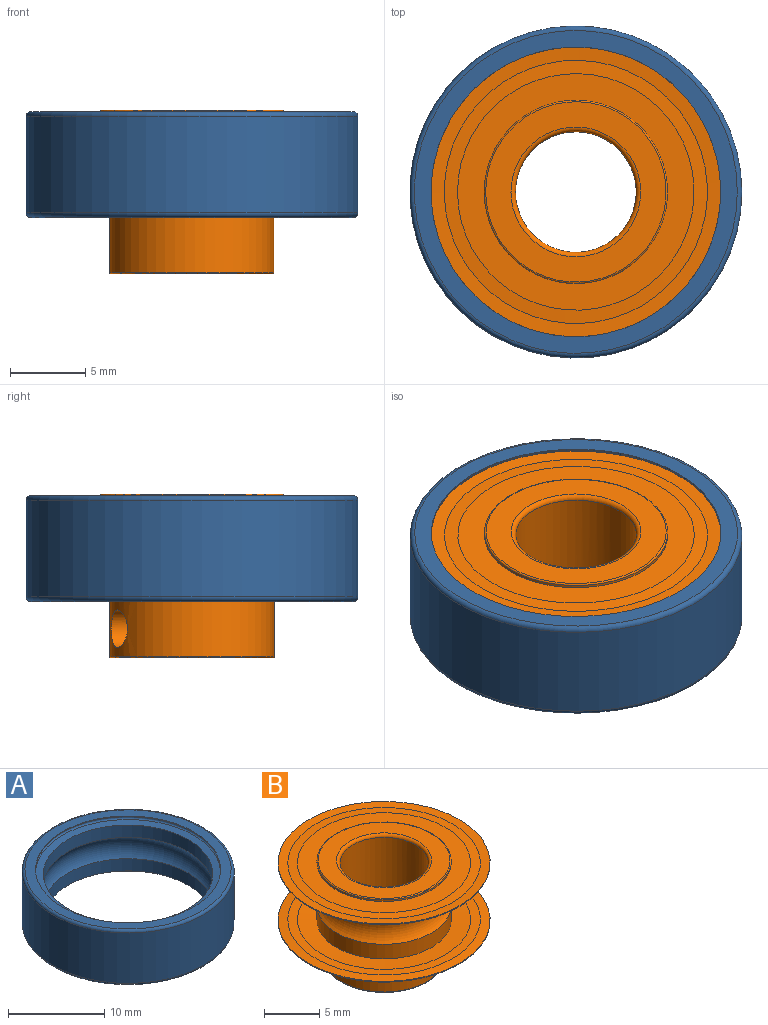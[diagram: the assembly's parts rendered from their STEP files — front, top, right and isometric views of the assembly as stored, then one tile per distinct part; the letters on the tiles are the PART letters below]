
ASSEMBLY  parts=2 mates=1
PART A: 14 faces, bbox 23.8x23.8x7 mm
  f0: torus R=10.7mm, axis (0,0,1), area 32.2mm2, adj f1,f13
  f1: cylinder r=11mm len=22mm, axis (0,0,1), area 442.3mm2, adj f0,f2
  f2: torus R=10.7mm, axis (0,0,1), area 32.2mm2, adj f1,f3
  f3: plane 21.4x21.4mm, normal (0,0,-1), area 70.2mm2, adj f2,f4
  f4: cylinder r=9.6mm len=19.2mm, axis (0,0,1), area 5.4mm2, adj f3,f5
  f5: torus R=9.6mm, axis (0,0,1), area 34.5mm2, adj f4,f6
  f6: cone r=8.8mm half-angle=80deg, axis (0,0,-1), area 47mm2, adj f5,f7
  f7: cylinder r=8.8mm len=17.6mm, axis (0,0,1), area 85.9mm2, adj f6,f8
  f8: torus R=7.35mm, axis (0,0,1), area 171.5mm2, adj f7,f9
  f9: cylinder r=8.8mm len=17.6mm, axis (0,0,1), area 85.9mm2, adj f8,f10
  f10: cone r=9.6mm half-angle=80deg, axis (0,0,1), area 47mm2, adj f9,f11
  f11: torus R=9.6mm, axis (0,0,1), area 34.5mm2, adj f10,f12
  f12: cylinder r=9.6mm len=19.2mm, axis (0,0,1), area 5.4mm2, adj f11,f13
  f13: plane 21.4x21.4mm, normal (0,0,1), area 70.2mm2, adj f0,f12
PART B: 32 faces, bbox 19.2x19.2x10.9 mm
  f0: torus R=7.35mm, axis (0,0,1), area 122.1mm2, adj f1,f29
  f1: cylinder r=6.07mm len=12.15mm, axis (0,0,1), area 61.8mm2, adj f0,f2
  f2: cone r=6.07mm half-angle=87.1deg, axis (0,0,-1), area 77.1mm2, adj f1,f3
  f3: plane 17.44x17.44mm, normal (0,0,-1), area 45.8mm2, adj f2,f4
  f4: cone r=8.72mm half-angle=84.2deg, axis (0,0,1), area 51mm2, adj f3,f5
  f5: cylinder r=9.6mm len=19.2mm, axis (0,0,1), area 5.4mm2, adj f4,f6
  f6: cone r=9.6mm half-angle=87.1deg, axis (0,0,1), area 50.8mm2, adj f5,f7
  f7: cone r=8.72mm half-angle=87.1deg, axis (0,0,-1), area 45.9mm2, adj f6,f8
  f8: plane 15.68x15.68mm, normal (0,0,1), area 77mm2, adj f7,f9
  f9: cylinder r=6.07mm len=12.15mm, axis (0,0,1), area 6.5mm2, adj f8,f10
  f10: torus R=5.98mm, axis (0,0,1), area 6mm2, adj f9,f11
  f11: plane 11.95x11.95mm, normal (0,0,1), area 54.1mm2, adj f10,f12
  f12: torus R=4.3mm, axis (0,0,1), area 12.2mm2, adj f11,f13
  f13: cylinder r=4mm len=10.25mm, axis (0,0,1), area 247.7mm2, adj f12,f14,f30,f31
  f14: torus R=4.3mm, axis (0,0,1), area 12.2mm2, adj f13,f15
  f15: plane 10.7x10.7mm, normal (0,0,-1), area 31.8mm2, adj f14,f16
  f16: torus R=5.35mm, axis (0,0,1), area 5.3mm2, adj f15,f17
  f17: cylinder r=5.45mm len=10.9mm, axis (0,0,1), area 115.1mm2, adj f16,f18,f30,f31
  f18: cone r=5.45mm half-angle=45deg, axis (0,0,1), area 4.9mm2, adj f17,f19
  f19: plane 11.95x11.95mm, normal (0,0,-1), area 15.4mm2, adj f18,f20
  f20: torus R=5.98mm, axis (0,0,1), area 6mm2, adj f19,f21
  f21: cylinder r=6.07mm len=12.15mm, axis (0,0,1), area 6.5mm2, adj f20,f22
  f22: plane 15.68x15.68mm, normal (0,0,-1), area 77mm2, adj f21,f23
  f23: cone r=7.84mm half-angle=87.1deg, axis (0,0,1), area 45.9mm2, adj f22,f24
  f24: cone r=8.72mm half-angle=87.1deg, axis (0,0,-1), area 50.8mm2, adj f23,f25
  f25: cylinder r=9.6mm len=19.2mm, axis (0,0,1), area 5.4mm2, adj f24,f26
  f26: cone r=9.6mm half-angle=84.2deg, axis (0,0,-1), area 51mm2, adj f25,f27
  f27: plane 17.44x17.44mm, normal (0,0,1), area 45.8mm2, adj f26,f28
  f28: cone r=7.84mm half-angle=87.1deg, axis (0,0,1), area 77.1mm2, adj f27,f29
  f29: cylinder r=6.07mm len=12.15mm, axis (0,0,1), area 61.8mm2, adj f0,f28
  f30: cylinder r=1.25mm len=2.5mm, axis (0,1,0), area 11.6mm2, adj f13,f17
  f31: cylinder r=1.25mm len=2.5mm, axis (1,0,0), area 11.6mm2, adj f13,f17
PLACE A t=(0,0,-19.33)mm
PLACE B rot(axis=(0,0,1),25deg) t=(0,0,-19.21)mm
MATE revolute A.f0 <-> B.f0  axis (0,0,-1) through (0,0,-22.31)mm
